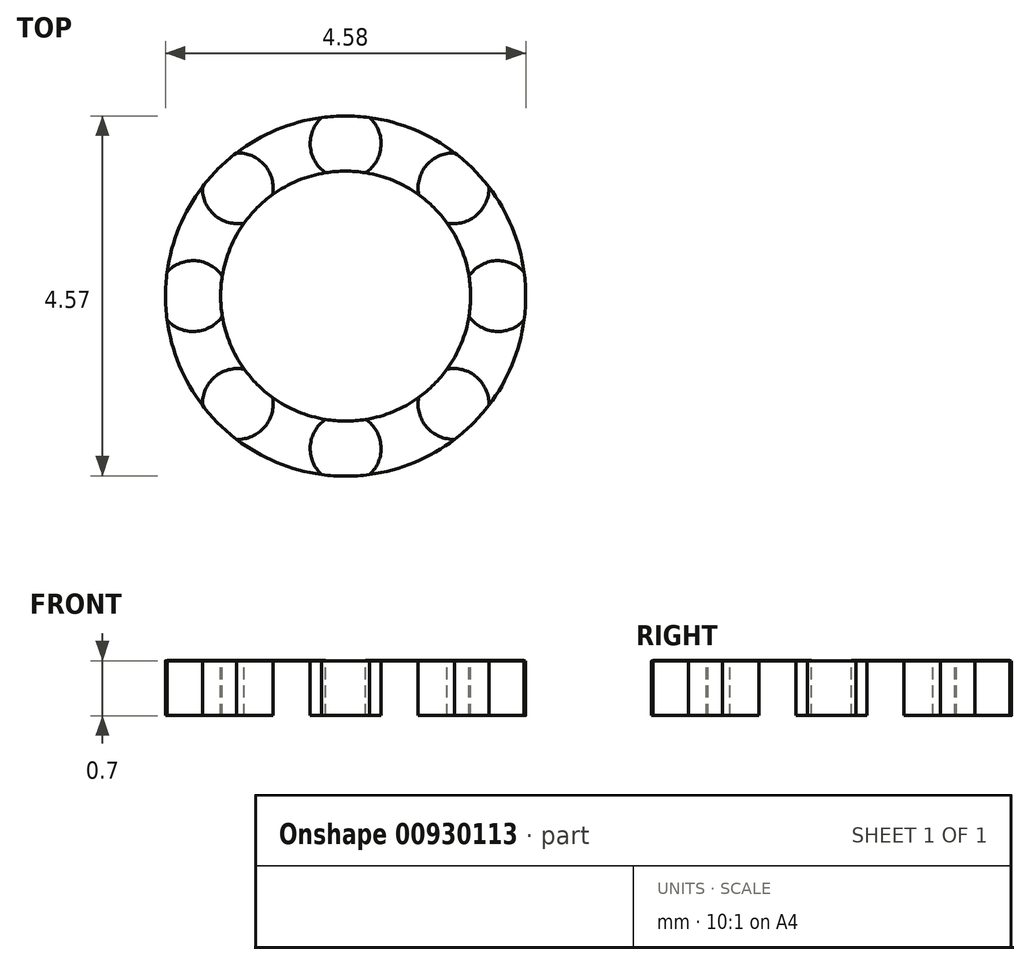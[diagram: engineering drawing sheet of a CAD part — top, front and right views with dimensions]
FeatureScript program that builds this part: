
annotation { "Feature Type Name" : "Feature", "Feature Type Description" : "" }
export const myFeature = defineFeature(function(context is Context, id is Id, definition is map)
    precondition{}
    {
        {
            var Q0;
            Q0=qCreatedBy(makeId("Top.planeOp"),FACE);
            var sketch = newSketch(context, id + "F0", { "sketchPlane" : qUnion([Q0])});
            skCircle(sketch, "E0", {"center": v(0, 0) * mm, "radius": 2 * mm});
            skCircle(sketch, "E1", {"center": v(1, 0) * mm, "radius": 0.5 * mm});
            skCircle(sketch, "E2.1.0", {"center": v(0.5, 0.87) * mm, "radius": 0.5 * mm});
            skCircle(sketch, "E2.2.0", {"center": v(-0.5, 0.87) * mm, "radius": 0.5 * mm});
            skCircle(sketch, "E2.3.0", {"center": v(-1, 0) * mm, "radius": 0.5 * mm});
            skCircle(sketch, "E2.4.0", {"center": v(-0.5, -0.87) * mm, "radius": 0.5 * mm});
            skCircle(sketch, "E2.5.0", {"center": v(0.5, -0.87) * mm, "radius": 0.5 * mm});
            skCircle(sketch, "E3", {"center": v(0, -6.29) * mm, "radius": 1.59 * mm});
            skCircle(sketch, "E4", {"center": v(0, -6.29) * mm, "radius": 2.29 * mm});
            skCircle(sketch, "E5", {"center": v(0, -8.22) * mm, "radius": 0.45 * mm});
            skCircle(sketch, "E6.1.0", {"center": v(1.37, -7.66) * mm, "radius": 0.45 * mm});
            skCircle(sketch, "E6.2.0", {"center": v(1.94, -6.29) * mm, "radius": 0.45 * mm});
            skLineSegment(sketch, "E7", {"start": v(0, -7.88) * mm, "end": v(0, -8.57) * mm, "construction": true});
            skCircle(sketch, "E8.1.3.0", {"center": v(1.37, -4.92) * mm, "radius": 0.45 * mm});
            skCircle(sketch, "E8.1.4.0", {"center": v(0, -4.35) * mm, "radius": 0.45 * mm});
            skCircle(sketch, "E8.1.5.0", {"center": v(-1.37, -4.92) * mm, "radius": 0.45 * mm});
            skCircle(sketch, "E8.1.6.0", {"center": v(-1.94, -6.29) * mm, "radius": 0.45 * mm});
            skCircle(sketch, "E9.1.7.0", {"center": v(-1.37, -7.66) * mm, "radius": 0.45 * mm});
            skSolve(sketch);
        }
        {
            var Q0;
            {var subQ0=sQuery(id+"F0.wireOp",EDGE,"E8.1.5.0");var subQ1=sQuery(id+"F0.wireOp",EDGE,"E3");var subQ2=makeQuery(id+"F0.imprint","INTERSECT",VERTEX,{"disambiguationData":[OD(1.0)],"derivedFrom":[subQ1,subQ0]});Q0=makeQuery(id+"F0.imprint","IMPRINT",FACE,{"disambiguationData":[TD([[makeQuery(id+"F0.imprint","IMPRINT",EDGE,{"disambiguationData":[TD([[subQ2,-1.0]])],"derivedFrom":subQ1}),-1.0]])]});}
            var Q1;
            {var subQ0=sQuery(id+"F0.wireOp",EDGE,"E8.1.4.0");var subQ1=sQuery(id+"F0.wireOp",EDGE,"E3");var subQ2=makeQuery(id+"F0.imprint","INTERSECT",VERTEX,{"disambiguationData":[OD(1.0)],"derivedFrom":[subQ1,subQ0]});Q1=makeQuery(id+"F0.imprint","IMPRINT",FACE,{"disambiguationData":[TD([[makeQuery(id+"F0.imprint","IMPRINT",EDGE,{"disambiguationData":[TD([[subQ2,-1.0]])],"derivedFrom":subQ1}),-1.0]])]});}
            var Q2;
            {var subQ0=sQuery(id+"F0.wireOp",EDGE,"E8.1.3.0");var subQ1=sQuery(id+"F0.wireOp",EDGE,"E3");var subQ2=makeQuery(id+"F0.imprint","INTERSECT",VERTEX,{"disambiguationData":[OD(1.0)],"derivedFrom":[subQ1,subQ0]});Q2=makeQuery(id+"F0.imprint","IMPRINT",FACE,{"disambiguationData":[TD([[makeQuery(id+"F0.imprint","IMPRINT",EDGE,{"disambiguationData":[TD([[subQ2,-1.0]])],"derivedFrom":subQ1}),-1.0]])]});}
            var Q3;
            {var subQ0=sQuery(id+"F0.wireOp",EDGE,"E8.1.3.0");var subQ1=sQuery(id+"F0.wireOp",EDGE,"E3");var subQ2=makeQuery(id+"F0.imprint","INTERSECT",VERTEX,{"disambiguationData":[OD(0.0)],"derivedFrom":[subQ1,subQ0]});Q3=makeQuery(id+"F0.imprint","IMPRINT",FACE,{"disambiguationData":[TD([[makeQuery(id+"F0.imprint","IMPRINT",EDGE,{"disambiguationData":[TD([[subQ2,1.0]])],"derivedFrom":subQ1}),-1.0]])]});}
            var Q4;
            {var subQ0=sQuery(id+"F0.wireOp",EDGE,"E6.1.0");var subQ1=sQuery(id+"F0.wireOp",EDGE,"E3");var subQ2=makeQuery(id+"F0.imprint","INTERSECT",VERTEX,{"disambiguationData":[OD(1.0)],"derivedFrom":[subQ1,subQ0]});Q4=makeQuery(id+"F0.imprint","IMPRINT",FACE,{"disambiguationData":[TD([[makeQuery(id+"F0.imprint","IMPRINT",EDGE,{"disambiguationData":[TD([[subQ2,-1.0]])],"derivedFrom":subQ1}),-1.0]])]});}
            var Q5;
            {var subQ0=sQuery(id+"F0.wireOp",EDGE,"E5");var subQ1=sQuery(id+"F0.wireOp",EDGE,"E3");var subQ2=makeQuery(id+"F0.imprint","INTERSECT",VERTEX,{"disambiguationData":[OD(1.0)],"derivedFrom":[subQ1,subQ0]});Q5=makeQuery(id+"F0.imprint","IMPRINT",FACE,{"disambiguationData":[TD([[makeQuery(id+"F0.imprint","IMPRINT",EDGE,{"disambiguationData":[TD([[subQ2,-1.0]])],"derivedFrom":subQ1}),-1.0]])]});}
            var Q6;
            {var subQ0=sQuery(id+"F0.wireOp",EDGE,"E9.1.7.0");var subQ1=sQuery(id+"F0.wireOp",EDGE,"E3");var subQ2=makeQuery(id+"F0.imprint","INTERSECT",VERTEX,{"disambiguationData":[OD(1.0)],"derivedFrom":[subQ1,subQ0]});Q6=makeQuery(id+"F0.imprint","IMPRINT",FACE,{"disambiguationData":[TD([[makeQuery(id+"F0.imprint","IMPRINT",EDGE,{"disambiguationData":[TD([[subQ2,-1.0]])],"derivedFrom":subQ1}),-1.0]])]});}
            var Q7;
            {var subQ0=sQuery(id+"F0.wireOp",EDGE,"E8.1.6.0");var subQ1=sQuery(id+"F0.wireOp",EDGE,"E3");var subQ2=makeQuery(id+"F0.imprint","INTERSECT",VERTEX,{"disambiguationData":[OD(1.0)],"derivedFrom":[subQ1,subQ0]});Q7=makeQuery(id+"F0.imprint","IMPRINT",FACE,{"disambiguationData":[TD([[makeQuery(id+"F0.imprint","IMPRINT",EDGE,{"disambiguationData":[TD([[subQ2,-1.0]])],"derivedFrom":subQ1}),-1.0]])]});}
            extrude(context, id + "F1", {"entities" : qUnion([Q0, Q1, Q2, Q3, Q4, Q5, Q6, Q7]), "depth" : 1 / 203.2 * mm, "offsetDistance" : 25 * mm});
        }
        {
            var Q0;
            {var subQ0=sQuery(id+"F0.wireOp",EDGE,"E8.1.5.0");var subQ1=sQuery(id+"F0.wireOp",EDGE,"E3");var subQ2=makeQuery(id+"F0.imprint","INTERSECT",VERTEX,{"disambiguationData":[OD(0.0)],"derivedFrom":[subQ1,subQ0]});Q0=makeQuery(id+"F0.imprint","IMPRINT",FACE,{"disambiguationData":[TD([[makeQuery(id+"F0.imprint","IMPRINT",EDGE,{"disambiguationData":[TD([[subQ2,-1.0]])],"derivedFrom":subQ1}),-1.0]])]});}
            var Q1;
            {var subQ0=sQuery(id+"F0.wireOp",EDGE,"E8.1.4.0");var subQ1=sQuery(id+"F0.wireOp",EDGE,"E3");var subQ2=makeQuery(id+"F0.imprint","INTERSECT",VERTEX,{"disambiguationData":[OD(0.0)],"derivedFrom":[subQ1,subQ0]});Q1=makeQuery(id+"F0.imprint","IMPRINT",FACE,{"disambiguationData":[TD([[makeQuery(id+"F0.imprint","IMPRINT",EDGE,{"disambiguationData":[TD([[subQ2,-1.0]])],"derivedFrom":subQ1}),-1.0]])]});}
            var Q2;
            {var subQ0=sQuery(id+"F0.wireOp",EDGE,"E8.1.3.0");var subQ1=sQuery(id+"F0.wireOp",EDGE,"E3");var subQ2=makeQuery(id+"F0.imprint","INTERSECT",VERTEX,{"disambiguationData":[OD(0.0)],"derivedFrom":[subQ1,subQ0]});Q2=makeQuery(id+"F0.imprint","IMPRINT",FACE,{"disambiguationData":[TD([[makeQuery(id+"F0.imprint","IMPRINT",EDGE,{"disambiguationData":[TD([[subQ2,-1.0]])],"derivedFrom":subQ1}),-1.0]])]});}
            var Q3;
            {var subQ0=sQuery(id+"F0.wireOp",EDGE,"E6.2.0");var subQ1=sQuery(id+"F0.wireOp",EDGE,"E3");var subQ2=makeQuery(id+"F0.imprint","INTERSECT",VERTEX,{"disambiguationData":[OD(0.0)],"derivedFrom":[subQ1,subQ0]});Q3=makeQuery(id+"F0.imprint","IMPRINT",FACE,{"disambiguationData":[TD([[makeQuery(id+"F0.imprint","IMPRINT",EDGE,{"disambiguationData":[TD([[subQ2,1.0]])],"derivedFrom":subQ1}),-1.0]])]});}
            var Q4;
            {var subQ0=sQuery(id+"F0.wireOp",EDGE,"E6.1.0");var subQ1=sQuery(id+"F0.wireOp",EDGE,"E3");var subQ2=makeQuery(id+"F0.imprint","INTERSECT",VERTEX,{"disambiguationData":[OD(0.0)],"derivedFrom":[subQ1,subQ0]});Q4=makeQuery(id+"F0.imprint","IMPRINT",FACE,{"disambiguationData":[TD([[makeQuery(id+"F0.imprint","IMPRINT",EDGE,{"disambiguationData":[TD([[subQ2,-1.0]])],"derivedFrom":subQ1}),-1.0]])]});}
            var Q5;
            {var subQ0=sQuery(id+"F0.wireOp",EDGE,"E5");var subQ1=sQuery(id+"F0.wireOp",EDGE,"E3");var subQ2=makeQuery(id+"F0.imprint","INTERSECT",VERTEX,{"disambiguationData":[OD(0.0)],"derivedFrom":[subQ1,subQ0]});Q5=makeQuery(id+"F0.imprint","IMPRINT",FACE,{"disambiguationData":[TD([[makeQuery(id+"F0.imprint","IMPRINT",EDGE,{"disambiguationData":[TD([[subQ2,-1.0]])],"derivedFrom":subQ1}),-1.0]])]});}
            var Q6;
            {var subQ0=sQuery(id+"F0.wireOp",EDGE,"E9.1.7.0");var subQ1=sQuery(id+"F0.wireOp",EDGE,"E3");var subQ2=makeQuery(id+"F0.imprint","INTERSECT",VERTEX,{"disambiguationData":[OD(0.0)],"derivedFrom":[subQ1,subQ0]});Q6=makeQuery(id+"F0.imprint","IMPRINT",FACE,{"disambiguationData":[TD([[makeQuery(id+"F0.imprint","IMPRINT",EDGE,{"disambiguationData":[TD([[subQ2,-1.0]])],"derivedFrom":subQ1}),-1.0]])]});}
            var Q7;
            {var subQ0=sQuery(id+"F0.wireOp",EDGE,"E8.1.6.0");var subQ1=sQuery(id+"F0.wireOp",EDGE,"E3");var subQ2=makeQuery(id+"F0.imprint","INTERSECT",VERTEX,{"disambiguationData":[OD(0.0)],"derivedFrom":[subQ1,subQ0]});Q7=makeQuery(id+"F0.imprint","IMPRINT",FACE,{"disambiguationData":[TD([[makeQuery(id+"F0.imprint","IMPRINT",EDGE,{"disambiguationData":[TD([[subQ2,-1.0]])],"derivedFrom":subQ1}),-1.0]])]});}
            extrude(context, id + "F2", {"entities" : qUnion([Q0, Q1, Q2, Q3, Q4, Q5, Q6, Q7]), "operationType" : NewBodyOperationType.ADD, "depth" : 1 / 203.2 * mm - .7 * mm, "offsetDistance" : 25 * mm});
        }
    });
